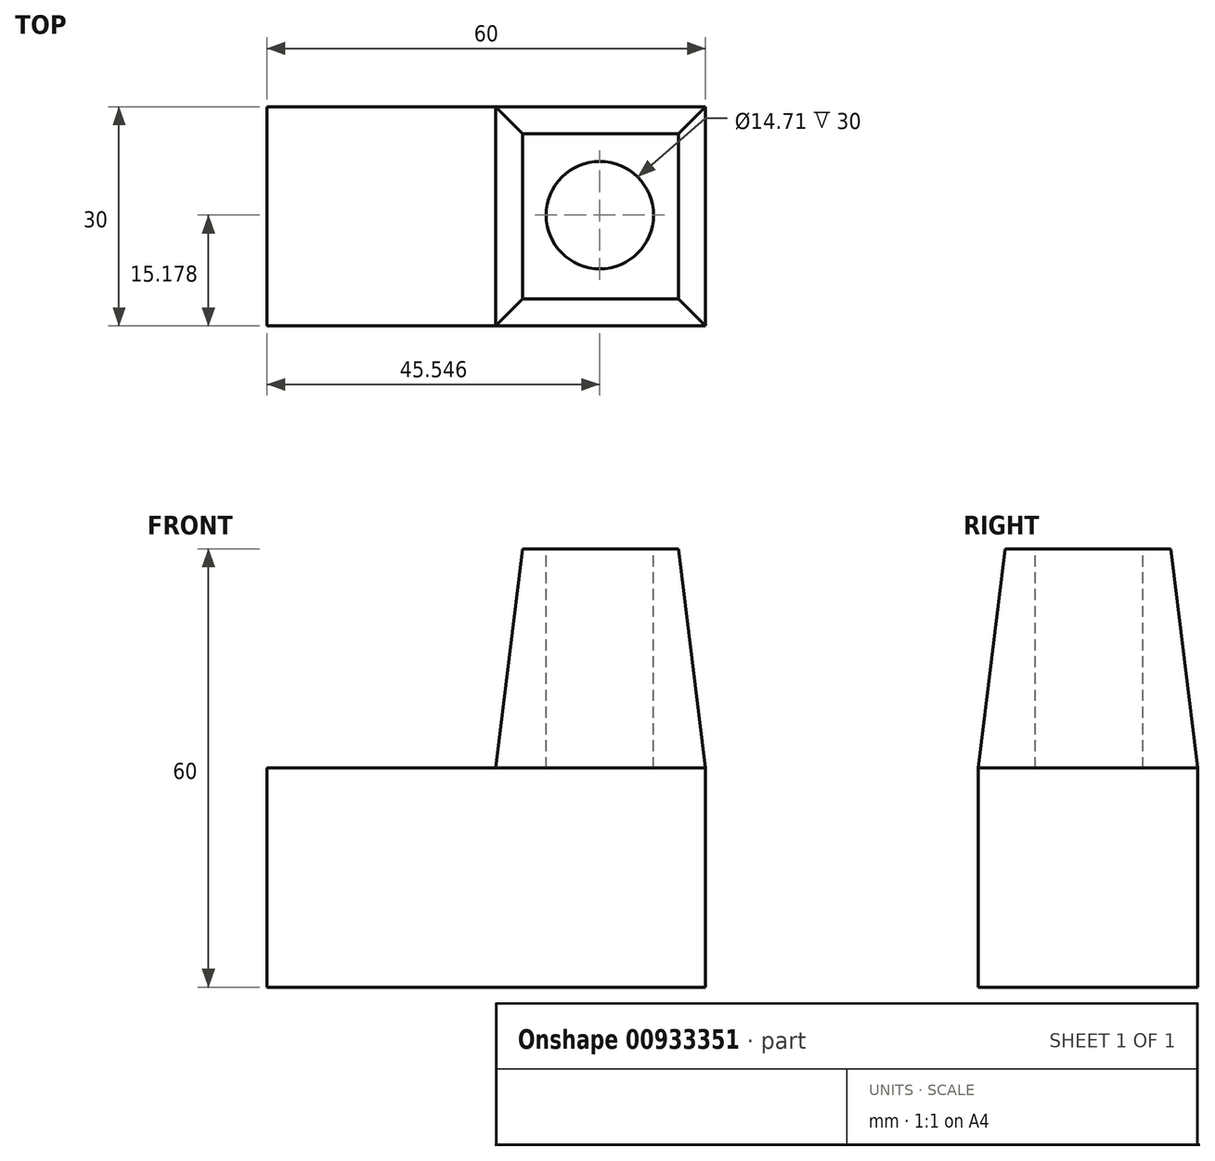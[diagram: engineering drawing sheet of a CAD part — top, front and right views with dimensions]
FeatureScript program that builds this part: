
annotation { "Feature Type Name" : "Feature", "Feature Type Description" : "" }
export const myFeature = defineFeature(function(context is Context, id is Id, definition is map)
    precondition{}
    {
        {
            var Q0;
            Q0=qCreatedBy(makeId("Front.planeOp"),FACE);
            var sketch = newSketch(context, id + "F0", { "sketchPlane" : qUnion([Q0])});
            skLineSegment(sketch, "E0.bottom", {"start": v(-31.3, 17) * mm, "end": v(28.7, 17) * mm});
            skLineSegment(sketch, "E0.top", {"start": v(-31.3, -13) * mm, "end": v(28.7, -13) * mm});
            skLineSegment(sketch, "E0.left", {"start": v(-31.3, 17) * mm, "end": v(-31.3, -13) * mm});
            skLineSegment(sketch, "E0.right", {"start": v(28.7, 17) * mm, "end": v(28.7, -13) * mm});
            skSolve(sketch);
        }
        {
            var Q0;
            Q0=makeQuery(id+"F0.imprint","IMPRINT",FACE,{"disambiguationData":[TD([[makeQuery(id+"F0.imprint","IMPRINT",EDGE,{"derivedFrom":sQuery(id+"F0.wireOp",EDGE,"E0.bottom")}),-1.0]])]});
            extrude(context, id + "F1", {"entities" : qUnion([Q0]), "depth" : 30 * mm, "offsetDistance" : 25.4 * mm});
        }
        {
            var Q0;
            Q0=makeQuery(id+"F1.opExtrude","SWEPT_FACE",FACE,{"disambiguationData":[OSD([sQuery(id+"F0.wireOp",EDGE,"E0.bottom")])]});
            var sketch = newSketch(context, id + "F2", { "sketchPlane" : qUnion([Q0])});
            skLineSegment(sketch, "E1.bottom", {"start": v(28.7, 0) * mm, "end": v(0, 0) * mm});
            skLineSegment(sketch, "E1.top", {"start": v(28.7, -30) * mm, "end": v(0, -30) * mm});
            skLineSegment(sketch, "E1.left", {"start": v(28.7, 0) * mm, "end": v(28.7, -30) * mm});
            skLineSegment(sketch, "E1.right", {"start": v(0, 0) * mm, "end": v(0, -30) * mm});
            skSolve(sketch);
        }
        {
            var Q0;
            Q0 = qSketchRegion(id + "F2", true);
            extrude(context, id + "F3", {"entities" : qUnion([Q0]), "operationType" : NewBodyOperationType.ADD, "depth" : 30 * mm, "offsetDistance" : 25.4 * mm, "hasDraft" : true, "draftAngle" : 7 * degree, "draftPullDirection" : true});
        }
        {
            var Q0;
            Q0=makeQuery(id+"F3.opExtrude","CAP_FACE",FACE,{"disambiguationData":[OSD([sQuery(id+"F2.wireOp",EDGE,"E1.bottom"),sQuery(id+"F2.wireOp",EDGE,"E1.top"),sQuery(id+"F2.wireOp",EDGE,"E1.left"),sQuery(id+"F2.wireOp",EDGE,"E1.right")])],"isStart":false});
            var sketch = newSketch(context, id + "F4", { "sketchPlane" : qUnion([Q0])});
            skCircle(sketch, "E2", {"center": v(14.25, -14.82) * mm, "radius": 7.35 * mm});
            skSolve(sketch);
        }
        {
            var Q0;
            Q0=makeQuery(id+"F4.imprint","IMPRINT",FACE,{"disambiguationData":[TD([[makeQuery(id+"F4.imprint","IMPRINT",EDGE,{"derivedFrom":sQuery(id+"F4.wireOp",EDGE,"E2")}),1.0]])]});
            extrude(context, id + "F5", {"entities" : qUnion([Q0]), "operationType" : NewBodyOperationType.REMOVE, "oppositeDirection" : true, "depth" : 30 * mm, "offsetDistance" : 25.4 * mm});
        }
    });
